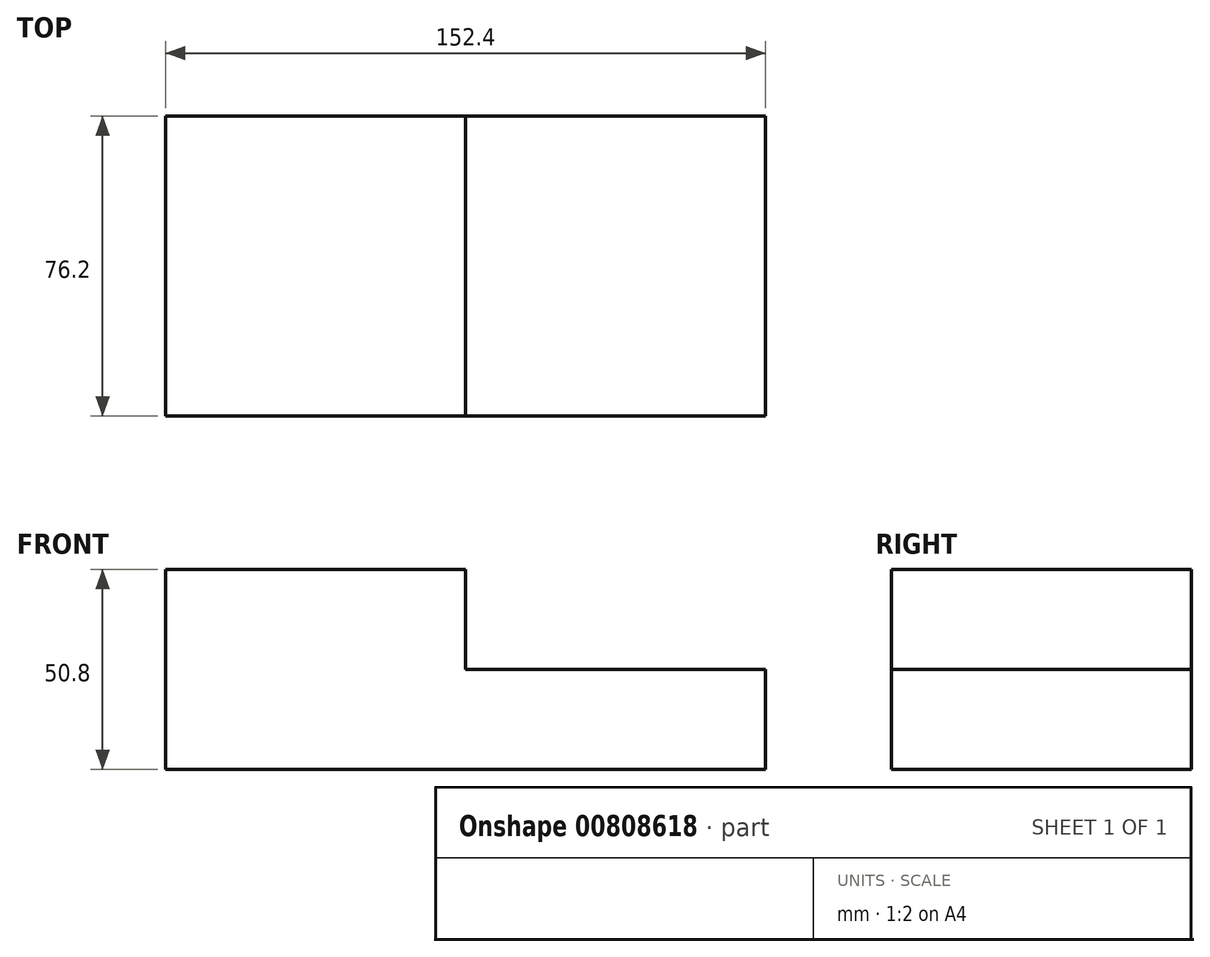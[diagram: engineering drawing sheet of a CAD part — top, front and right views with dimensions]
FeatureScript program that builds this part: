
annotation { "Feature Type Name" : "Feature", "Feature Type Description" : "" }
export const myFeature = defineFeature(function(context is Context, id is Id, definition is map)
    precondition{}
    {
        {
            var Q0;
            Q0=qCreatedBy(makeId("Front.planeOp"),FACE);
            var sketch = newSketch(context, id + "F0", { "sketchPlane" : qUnion([Q0])});
            skLineSegment(sketch, "E0", {"start": v(0, 0) * mm, "end": v(152.4, 0) * mm});
            skLineSegment(sketch, "E1", {"start": v(0, 0) * mm, "end": v(0, 50.8) * mm});
            skLineSegment(sketch, "E2", {"start": v(0, 50.8) * mm, "end": v(76.2, 50.8) * mm});
            skLineSegment(sketch, "E3", {"start": v(76.2, 50.8) * mm, "end": v(76.2, 25.4) * mm});
            skLineSegment(sketch, "E4", {"start": v(76.2, 25.4) * mm, "end": v(152.4, 25.4) * mm});
            skLineSegment(sketch, "E5", {"start": v(152.4, 25.4) * mm, "end": v(152.4, 0) * mm});
            skSolve(sketch);
        }
        {
            var Q0;
            Q0=makeQuery(id+"F0.imprint","IMPRINT",FACE,{"disambiguationData":[TD([[makeQuery(id+"F0.imprint","IMPRINT",EDGE,{"derivedFrom":sQuery(id+"F0.wireOp",EDGE,"E0")}),1.0]])]});
            extrude(context, id + "F1", {"entities" : qUnion([Q0]), "depth" : 76.2 * mm, "offsetDistance" : 25.4 * mm});
        }
    });
